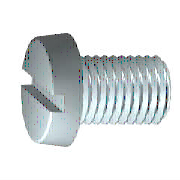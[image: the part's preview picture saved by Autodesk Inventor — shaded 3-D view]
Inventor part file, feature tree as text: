
AUTODESK INVENTOR PART (.ipt)
format: ipt  version: 2023 (Build 270158000, 158)  size: 180,736 bytes
history: native  units: mm (DEFAULTED — no unit token found)
features: sketch x2, extrude x1, plane x1
ambient origin geometry x7: Origin, YZ Plane, XZ Plane, X Axis, Y Axis, Z Axis, Center Point
bodies: Solid1 (feature_tree), Body (feature_tree)
feature tree (4):
  sketch  "Sketch2"  dims[d2=0.49086mm d3=3.3mm d4=5.0mm d5=4.566987mm d8=90.0deg d7=0.0mm d9=8.5mm d10=0.872665mm d11=1.2mm d12=8.5mm d14=0.2mm d15=23.4mm d16=0.0mm d17=0.433015mm d18=0.49086mm d19=1.3mm d20=0.0mm d36=45.0deg d37=0.0mm d39=0.0mm]
  extrude  "Slot"  Depth=23.4mm
  plane  "Work Plane1"
  sketch  "Sketch1"  dims[d0=25.0mm d1=23.4mm]
